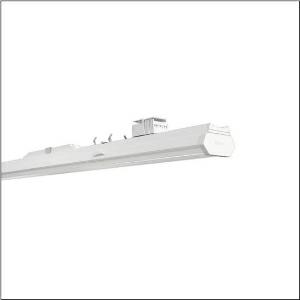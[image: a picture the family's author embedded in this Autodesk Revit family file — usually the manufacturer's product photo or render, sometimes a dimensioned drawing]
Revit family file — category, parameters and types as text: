
# Revit family: licross_r__21_protected_ho_52tp12dn4e5m_9624
name_source: partatom
category: Lighting Fixtures
units: mm (PartAtom-declared; Revit-internal decimal feet)

## family parameters
Cut with Voids When Loaded = No
Host = Face
Light Source = No
Part Type = Normal
Room Calculation Point = No
Round Connector Dimension = Use Diameter
Shared = No

## types (1)
- --- (1 x LED, 14690 lm, 84.9 W, 4000K)
    Apparent Load = 85 VA
    CIE Flux Codes = 70 91 97 98 100
    Color Rendering = 80
    Color Temperature = 4000K
    Default Elevation = 1800 mm
    Description = Licross® 21 Protected HO, luminaire insert, of sheet steel, galvanised, coil coated, white, length: 1.500mm, width: 90mm, height: 103mm, LED rated luminous flux: 14.690lm, light colour: 840, control gear: DALI 2, with plug, 5-pole, with phase selection, mains connection: 220..240V, AC, 50/60Hz, rated input power: 85W, internal wiring halogen-free, primary light control with lens, of plastic, primary optical cover: cover, of PMMA, light emission: direct distribution, primary light characteristic: symmetric, protection rating (complete): IP64, insulation class (complete): insulation class I (protective earthing), certification: CE, ENEC, VDE, UKCA, protection symbol: D if used in an environment with conductive dust loads with corresponding accessories, impact resistance: IK06, permissible ambient temperature for indoor applications: -25..+35°C, corresponds to IFS (International Featured Standards) requirements for safety and quality in the food industry, reducing of maximum allowable ambient temperature of 5°C with ceiling mounting, LABS conformity tested according to VDMA 24364:2018-05, packaging unit: 1 piece
    Height = 92 mm
    Lamp = 1 x LED
    Lamp Light Flux = 14690 lm
    Lamp Power = 84.9 W
    Lamp count = 1
    Length = 1500 mm
    Luminous efficacy = 173 lm/W
    Manufacturer = Siteco
    ModVariant = No
    Model = 52TP12DN4E5M
    Mounting Place = Ceiling
    Mounting Type = Pendant
    Number of Poles = 1
    OnlyDefault = Yes
    Power Factor = 1
    Product Name = Licross® 21 Protected HO
    Product group = luminaire insert | ceiling pendant
    ProductGroupID = 902
    Protection Class = Protection class I
    Protection Degree = IP 64
    RLX_Detail_Level = 1
    RLX_Emergency_Light_Flux = 0 lm
    RLX_Emergency_Type = 0
    RLX_Emergency_Type_DB = No
    RlxData = <blob elided: 24457 chars, md5=ac40befb>
    Socket = socket
    Standby Power = 0 W
    System Light Flux = 14690 lm
    System Power = 85 W
    Type Comments = factory setting: luminous flux: 100 % | dim-lin: 254 | 484 mA
    Type Image = l_1256148.jpg
    URL = http://relux.com
    VarID = @adj_150407
    Voltage = 0 V
    Weight = 0.00 kg
    Width = 88 mm

## geometry (parser evidence)
native form markers: Blend x4, Sweep x10
no freeform markers — native parametric forms only
